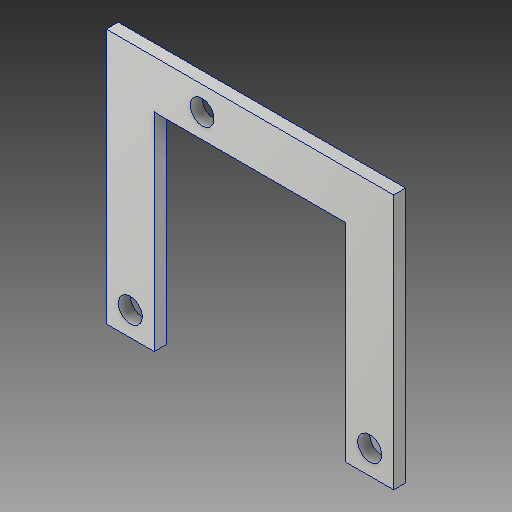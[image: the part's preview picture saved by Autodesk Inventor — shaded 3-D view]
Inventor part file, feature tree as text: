
AUTODESK INVENTOR PART (.ipt)
format: ipt  version: 2018.1 (Build 221171000, 171)  size: 125,440 bytes
history: native  units: mm
features: extrude x2, sketch x2, other x1
ambient origin geometry x8: Origin, YZ Plane, XZ Plane, XY Plane, X Axis, Y Axis, Z Axis, Center Point
bodies: Body1 (feature_tree)
feature tree (5):
  other  "ソリッド1"
  extrude  "押し出し1"  Depth=20.0mm
  extrude  "押し出し2"  Depth=20.0mm
  sketch  "スケッチ1"
  sketch  "スケッチ2"
